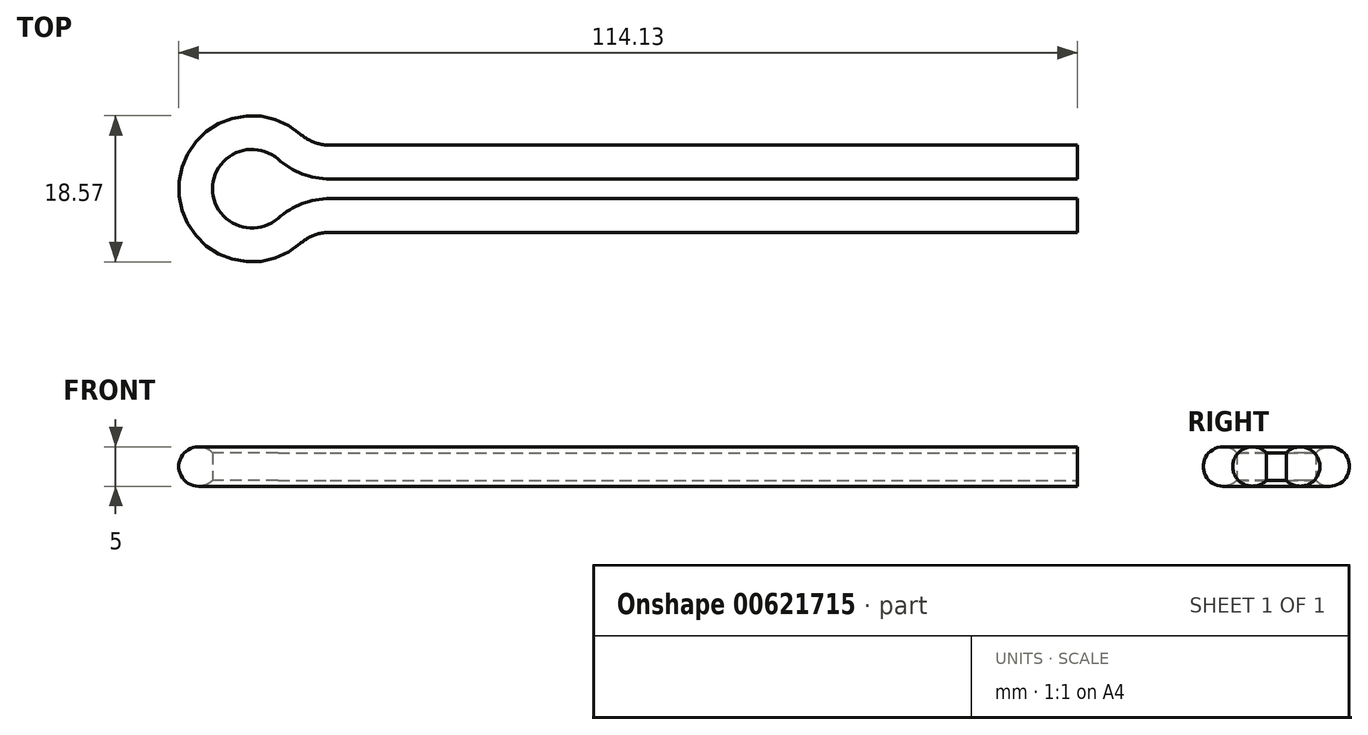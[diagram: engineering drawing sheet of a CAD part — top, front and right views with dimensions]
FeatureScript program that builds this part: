
annotation { "Feature Type Name" : "Feature", "Feature Type Description" : "" }
export const myFeature = defineFeature(function(context is Context, id is Id, definition is map)
    precondition{}
    {
        {
            var Q0;
            Q0=qCreatedBy(makeId("Top.planeOp"),FACE);
            var sketch = newSketch(context, id + "F0", { "sketchPlane" : qUnion([Q0])});
            skLineSegment(sketch, "E0", {"start": v(67.85, 27.15) * mm, "end": v(-27.07, 27.15) * mm});
            skLineSegment(sketch, "E1", {"start": v(67.85, 24.65) * mm, "end": v(-27.07, 24.65) * mm});
            skArc(sketch, "E2", {"start": v(-33.69, 29.65) * mm, "mid": v(-42, 25.9) * mm, "end": v(-33.69, 22.15) * mm});
            skPoint(sketch, "E3.visualSharp", {"position": v(-32.15, 27.15) * mm});
            skArc(sketch, "E3.filletArc", {"start": v(-33.69, 29.65) * mm, "mid": v(-30.6, 27.8) * mm, "end": v(-27.07, 27.15) * mm});
            skPoint(sketch, "E4.visualSharp", {"position": v(-32.15, 24.65) * mm});
            skArc(sketch, "E4.filletArc", {"start": v(-27.07, 24.65) * mm, "mid": v(-30.6, 24) * mm, "end": v(-33.69, 22.15) * mm});
            skSolve(sketch);
        }
        {
            var Q0;
            Q0=sQuery(id+"F0.wireOp",VERTEX,"E1.start");
            var Q1;
            Q1=qCreatedBy(makeId("Right.planeOp"),FACE);
            cPlane(context, id + "F1", {"entities" : qUnion([Q0, Q1]), "cplaneType" : CPlaneType.PLANE_POINT, "offset" : 25 * mm, "width" : 150 * mm, "height" : 150 * mm});
        }
        {
            var Q0;
            Q0=qCreatedBy(id+"F1.planeOp",FACE);
            var sketch = newSketch(context, id + "F2", { "sketchPlane" : qUnion([Q0])});
            skLineSegment(sketch, "E5", {"start": v(24.65, 0) * mm, "end": v(24.65, -3.5) * mm});
            skArc(sketch, "E6", {"start": v(24.65, 0) * mm, "mid": v(20.36, -1.75) * mm, "end": v(24.65, -3.5) * mm});
            skSolve(sketch);
        }
        {
            var Q0;
            Q0=qSketchRegion(id+"F2",true);
            var Q1;
            Q1=qConstructionFilter(qBodyType(qCreatedBy(id+"F0",EDGE),BodyType.WIRE),ConstructionObject.NO);
            sweep(context, id + "F3", {"profiles" : qUnion([Q0]), "path" : qUnion([Q1])});
        }
    });
